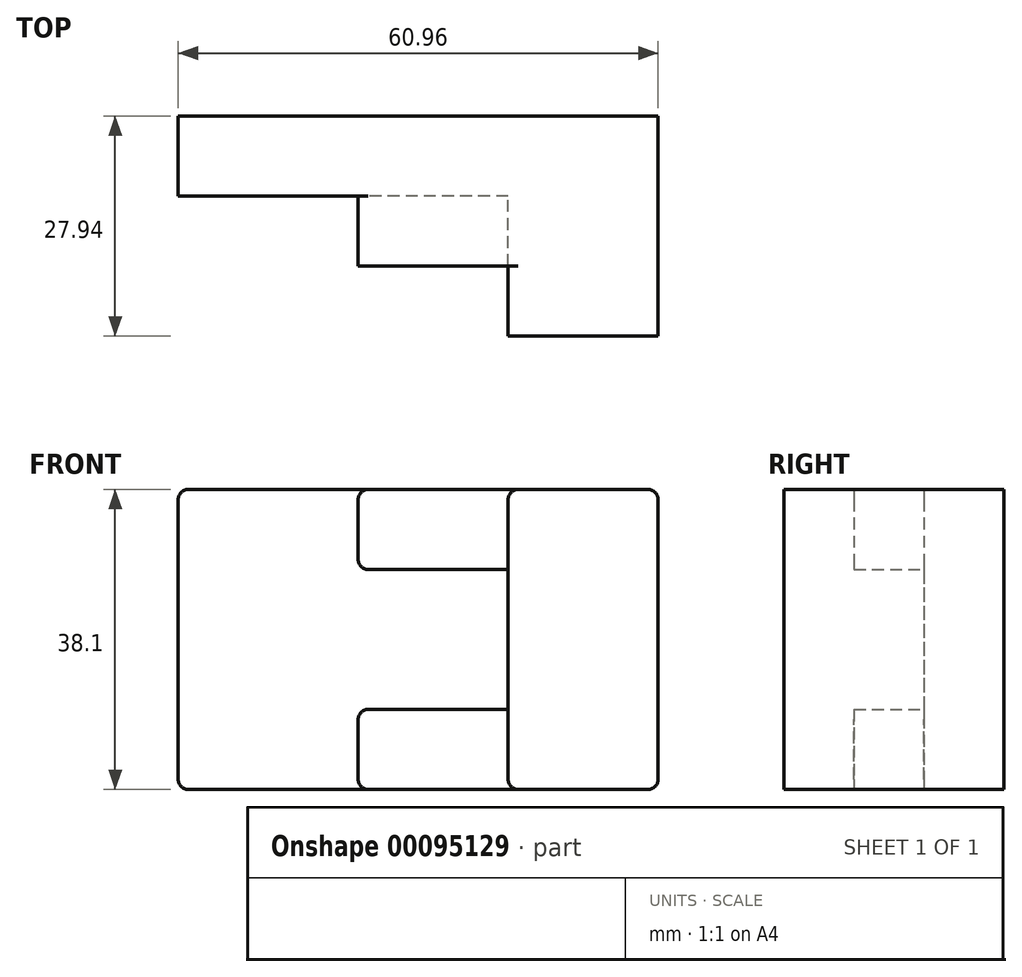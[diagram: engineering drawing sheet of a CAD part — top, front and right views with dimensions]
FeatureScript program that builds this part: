
annotation { "Feature Type Name" : "Feature", "Feature Type Description" : "" }
export const myFeature = defineFeature(function(context is Context, id is Id, definition is map)
    precondition{}
    {
        {
            var Q0;
            Q0=qCreatedBy(makeId("Front.planeOp"),FACE);
            var sketch = newSketch(context, id + "F0", { "sketchPlane" : qUnion([Q0])});
            skLineSegment(sketch, "E0.bottom", {"start": v(-30.48, 19.05) * mm, "end": v(30.48, 19.05) * mm});
            skLineSegment(sketch, "E0.top", {"start": v(-30.48, -19.05) * mm, "end": v(30.48, -19.05) * mm});
            skLineSegment(sketch, "E0.left", {"start": v(-30.48, 19.05) * mm, "end": v(-30.48, -19.05) * mm});
            skLineSegment(sketch, "E0.right", {"start": v(30.48, 19.05) * mm, "end": v(30.48, -19.05) * mm});
            skPoint(sketch, "E0.middle", {"position": v(0, 0) * mm});
            skSolve(sketch);
        }
        {
            var Q0;
            Q0=makeQuery(id+"F0.imprint","IMPRINT",FACE,{"disambiguationData":[TD([[makeQuery(id+"F0.imprint","IMPRINT",EDGE,{"derivedFrom":sQuery(id+"F0.wireOp",EDGE,"E0.bottom")}),-1.0]])]});
            extrude(context, id + "F1", {"entities" : qUnion([Q0]), "depth" : 10.16 * mm});
        }
        {
            var Q0;
            Q0=makeQuery(id+"F1.opExtrude","CAP_FACE",FACE,{"disambiguationData":[OSD([sQuery(id+"F0.wireOp",EDGE,"E0.bottom"),sQuery(id+"F0.wireOp",EDGE,"E0.top"),sQuery(id+"F0.wireOp",EDGE,"E0.left"),sQuery(id+"F0.wireOp",EDGE,"E0.right")])],"isStart":false});
            var sketch = newSketch(context, id + "F2", { "sketchPlane" : qUnion([Q0])});
            skLineSegment(sketch, "E1.bottom", {"start": v(11.43, 19.05) * mm, "end": v(30.48, 19.05) * mm});
            skLineSegment(sketch, "E1.top", {"start": v(11.43, -19.05) * mm, "end": v(30.48, -19.05) * mm});
            skLineSegment(sketch, "E1.left", {"start": v(11.43, 19.05) * mm, "end": v(11.43, -19.05) * mm});
            skLineSegment(sketch, "E1.right", {"start": v(30.48, 19.05) * mm, "end": v(30.48, -19.05) * mm});
            skSolve(sketch);
        }
        {
            var Q0;
            Q0 = qSketchRegion(id + "F2", true);
            extrude(context, id + "F3", {"entities" : qUnion([Q0]), "operationType" : NewBodyOperationType.ADD, "depth" : 17.78 * mm});
        }
        {
            var Q0;
            Q0=makeQuery(id+"F1.opExtrude","CAP_FACE",FACE,{"disambiguationData":[OSD([sQuery(id+"F0.wireOp",EDGE,"E0.bottom"),sQuery(id+"F0.wireOp",EDGE,"E0.top"),sQuery(id+"F0.wireOp",EDGE,"E0.left"),sQuery(id+"F0.wireOp",EDGE,"E0.right")])],"isStart":false});
            var sketch = newSketch(context, id + "F4", { "sketchPlane" : qUnion([Q0])});
            skLineSegment(sketch, "E2.bottom", {"start": v(11.43, 19.05) * mm, "end": v(-7.62, 19.05) * mm});
            skLineSegment(sketch, "E2.top", {"start": v(11.43, 8.9) * mm, "end": v(-7.62, 8.9) * mm});
            skLineSegment(sketch, "E2.left", {"start": v(11.43, 19.05) * mm, "end": v(11.43, 8.9) * mm});
            skLineSegment(sketch, "E2.right", {"start": v(-7.62, 19.05) * mm, "end": v(-7.62, 8.9) * mm});
            skLineSegment(sketch, "E3.bottom", {"start": v(11.43, -19.05) * mm, "end": v(-7.62, -19.05) * mm});
            skLineSegment(sketch, "E3.top", {"start": v(11.43, -8.89) * mm, "end": v(-7.62, -8.89) * mm});
            skLineSegment(sketch, "E3.left", {"start": v(11.43, -19.05) * mm, "end": v(11.43, -8.89) * mm});
            skLineSegment(sketch, "E3.right", {"start": v(-7.62, -19.05) * mm, "end": v(-7.62, -8.89) * mm});
            skSolve(sketch);
        }
        {
            var Q0;
            Q0 = qSketchRegion(id + "F4", true);
            extrude(context, id + "F5", {"entities" : qUnion([Q0]), "operationType" : NewBodyOperationType.ADD, "depth" : 8.9 * mm});
        }
        {
            var Q0;
            Q0=makeQuery(id+"F1.opExtrude","SWEPT_EDGE",EDGE,{"disambiguationData":[OSD([sQuery(id+"F0.wireOp",EDGE,"E0.bottom"),sQuery(id+"F0.wireOp",EDGE,"E0.left")])]});
            var Q1;
            Q1=makeQuery(id+"F1.opExtrude","SWEPT_EDGE",EDGE,{"disambiguationData":[OSD([sQuery(id+"F0.wireOp",EDGE,"E0.top"),sQuery(id+"F0.wireOp",EDGE,"E0.left")])]});
            var Q2;
            Q2=makeQuery(id+"F5.opExtrude","SWEPT_EDGE",EDGE,{"disambiguationData":[OSD([sQuery(id+"F0.wireOp",EDGE,"E0.bottom"),sQuery(id+"F4.wireOp",EDGE,"E2.bottom"),sQuery(id+"F4.wireOp",EDGE,"E2.right")])]});
            var Q3;
            Q3=makeQuery(id+"F5.opExtrude","SWEPT_EDGE",EDGE,{"disambiguationData":[OSD([sQuery(id+"F4.wireOp",EDGE,"E2.top"),sQuery(id+"F4.wireOp",EDGE,"E2.right")])]});
            var Q4;
            Q4=makeQuery(id+"F5.opExtrude","SWEPT_EDGE",EDGE,{"disambiguationData":[OSD([sQuery(id+"F4.wireOp",EDGE,"E3.top"),sQuery(id+"F4.wireOp",EDGE,"E3.right")])]});
            var Q5;
            Q5=makeQuery(id+"F5.opExtrude","SWEPT_EDGE",EDGE,{"disambiguationData":[OSD([sQuery(id+"F0.wireOp",EDGE,"E0.top"),sQuery(id+"F4.wireOp",EDGE,"E3.bottom"),sQuery(id+"F4.wireOp",EDGE,"E3.right")])]});
            var Q6;
            Q6=makeQuery(id+"F3.opExtrude","SWEPT_EDGE",EDGE,{"disambiguationData":[OSD([sQuery(id+"F0.wireOp",EDGE,"E0.top"),sQuery(id+"F2.wireOp",EDGE,"E1.top"),sQuery(id+"F2.wireOp",EDGE,"E1.left")])]});
            var Q7;
            Q7=makeQuery(id+"F3.opExtrude","SWEPT_EDGE",EDGE,{"disambiguationData":[OSD([sQuery(id+"F0.wireOp",EDGE,"E0.bottom"),sQuery(id+"F2.wireOp",EDGE,"E1.bottom"),sQuery(id+"F2.wireOp",EDGE,"E1.left")])]});
            var Q8;
            Q8=makeQuery(id+"F3.boolean.opBoolean","MERGE",EDGE,{"derivedFrom":[makeQuery(id+"F1.opExtrude","SWEPT_EDGE",EDGE,{"disambiguationData":[OSD([sQuery(id+"F0.wireOp",EDGE,"E0.bottom"),sQuery(id+"F0.wireOp",EDGE,"E0.right")])]}),makeQuery(id+"F3.opExtrude","SWEPT_EDGE",EDGE,{"disambiguationData":[OSD([sQuery(id+"F2.wireOp",EDGE,"E1.bottom"),sQuery(id+"F2.wireOp",EDGE,"E1.right")])]})]});
            var Q9;
            Q9=makeQuery(id+"F3.boolean.opBoolean","MERGE",EDGE,{"derivedFrom":[makeQuery(id+"F1.opExtrude","SWEPT_EDGE",EDGE,{"disambiguationData":[OSD([sQuery(id+"F0.wireOp",EDGE,"E0.top"),sQuery(id+"F0.wireOp",EDGE,"E0.right")])]}),makeQuery(id+"F3.opExtrude","SWEPT_EDGE",EDGE,{"disambiguationData":[OSD([sQuery(id+"F2.wireOp",EDGE,"E1.top"),sQuery(id+"F2.wireOp",EDGE,"E1.right")])]})]});
            var Q10;
            Q10=makeQuery(id+"F5.opExtrude","SWEPT_EDGE",EDGE,{"disambiguationData":[OSD([sQuery(id+"F2.wireOp",EDGE,"E1.left"),sQuery(id+"F4.wireOp",EDGE,"E3.top"),sQuery(id+"F4.wireOp",EDGE,"E3.left")])]});
            var Q11;
            Q11=makeQuery(id+"F5.opExtrude","SWEPT_EDGE",EDGE,{"disambiguationData":[OSD([sQuery(id+"F2.wireOp",EDGE,"E1.left"),sQuery(id+"F4.wireOp",EDGE,"E2.top"),sQuery(id+"F4.wireOp",EDGE,"E2.left")])]});
            fillet(context, id + "F6", {"entities" : qUnion([Q0, Q1, Q2, Q3, Q4, Q5, Q6, Q7, Q8, Q9, Q10, Q11]), "radius" : 1.27 * mm, "tangentPropagation" : true, "allowEdgeOverflow" : false});
        }
    });
